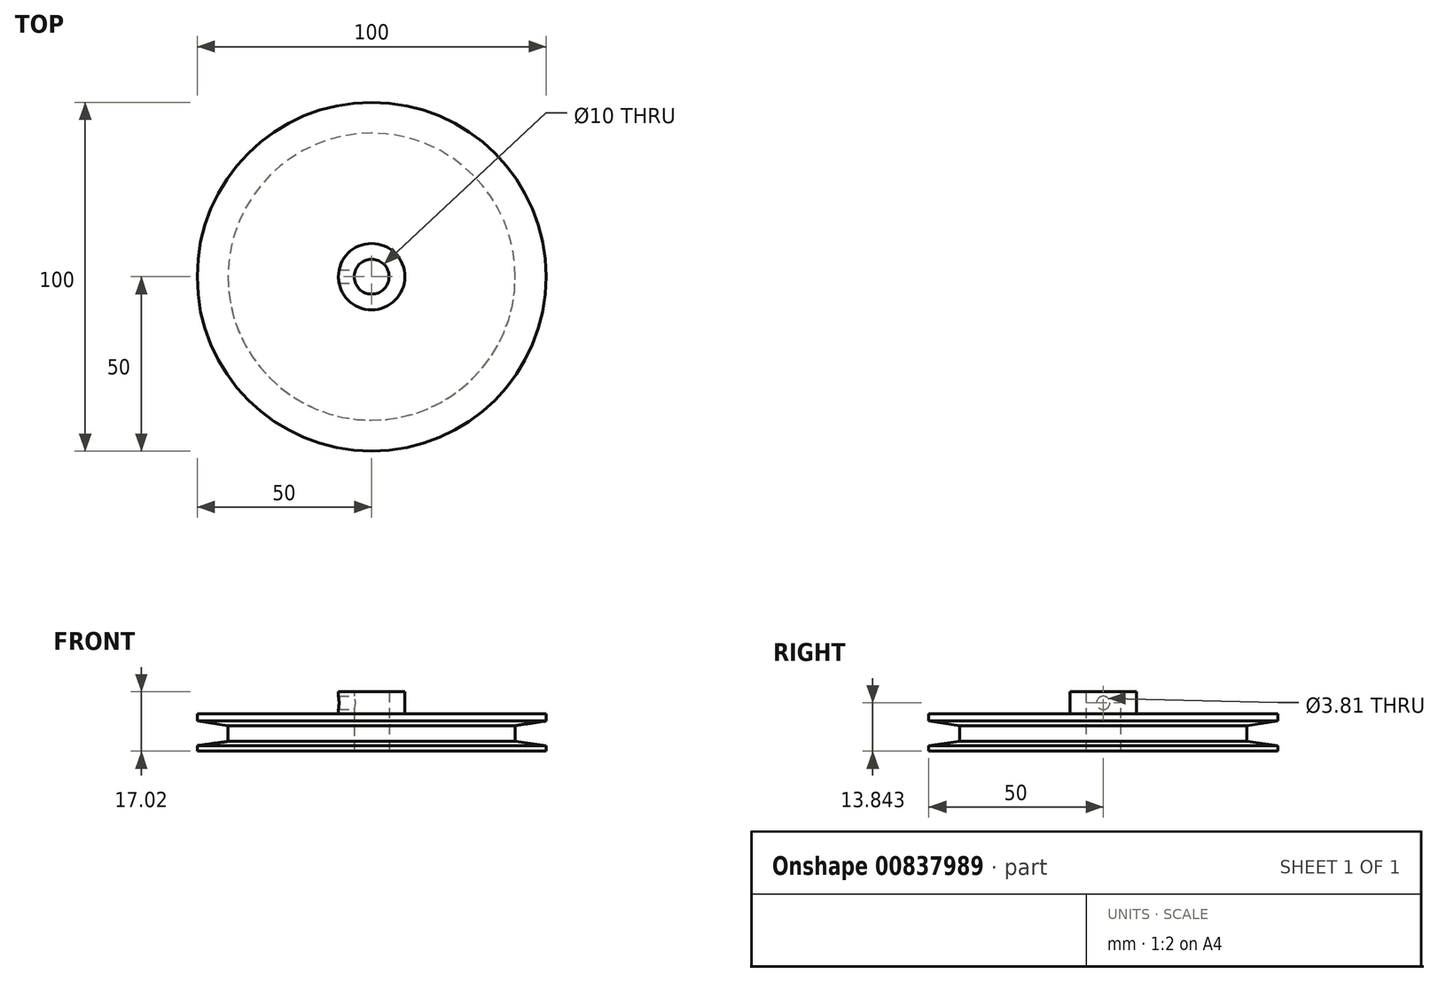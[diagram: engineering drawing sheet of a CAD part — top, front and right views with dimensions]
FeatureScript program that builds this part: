
annotation { "Feature Type Name" : "Feature", "Feature Type Description" : "" }
export const myFeature = defineFeature(function(context is Context, id is Id, definition is map)
    precondition{}
    {
        {
            var Q0;
            Q0=qCreatedBy(makeId("Top.planeOp"),FACE);
            var sketch = newSketch(context, id + "F0", { "sketchPlane" : qUnion([Q0])});
            skCircle(sketch, "E0", {"center": v(0, 0) * mm, "radius": 50 * mm});
            skSolve(sketch);
        }
        {
            var Q0;
            Q0=makeQuery(id+"F0.imprint","IMPRINT",FACE,{"disambiguationData":[TD([[makeQuery(id+"F0.imprint","IMPRINT",EDGE,{"derivedFrom":sQuery(id+"F0.wireOp",EDGE,"E0")}),1.0]])]});
            extrude(context, id + "F1", {"entities" : qUnion([Q0]), "depth" : 10.67 * mm, "offsetDistance" : 25.4 * mm});
        }
        {
            var Q0;
            Q0=makeQuery(id+"F1.opExtrude","CAP_FACE",FACE,{"disambiguationData":[OSD([sQuery(id+"F0.wireOp",EDGE,"E0")])],"isStart":false});
            var sketch = newSketch(context, id + "F2", { "sketchPlane" : qUnion([Q0])});
            skCircle(sketch, "E1", {"center": v(0, 0) * mm, "radius": 9.53 * mm});
            skSolve(sketch);
        }
        {
            var Q0;
            Q0=makeQuery(id+"F2.imprint","IMPRINT",FACE,{"disambiguationData":[TD([[makeQuery(id+"F2.imprint","IMPRINT",EDGE,{"derivedFrom":sQuery(id+"F2.wireOp",EDGE,"E1")}),1.0]])]});
            extrude(context, id + "F3", {"entities" : qUnion([Q0]), "operationType" : NewBodyOperationType.ADD, "depth" : 6.35 * mm, "offsetDistance" : 25.4 * mm});
        }
        {
            var Q0;
            Q0=qCreatedBy(makeId("Right.planeOp"),FACE);
            var sketch = newSketch(context, id + "F4", { "sketchPlane" : qUnion([Q0])});
            skCircle(sketch, "E2", {"center": v(0, 13.84) * mm, "radius": 1.9 * mm});
            skSolve(sketch);
        }
        {
            var Q0;
            Q0=qSketchRegion(id+"F4",true);
            extrude(context, id + "F5", {"entities" : qUnion([Q0]), "operationType" : NewBodyOperationType.REMOVE, "oppositeDirection" : true, "depth" : 25.4 * mm, "offsetDistance" : 25.4 * mm});
        }
        {
            var Q0;
            Q0=makeQuery(id+"F1.opExtrude","CAP_FACE",FACE,{"disambiguationData":[OSD([sQuery(id+"F0.wireOp",EDGE,"E0")])],"isStart":true});
            var sketch = newSketch(context, id + "F6", { "sketchPlane" : qUnion([Q0])});
            skCircle(sketch, "E3", {"center": v(0, 0) * mm, "radius": 5 * mm});
            skSolve(sketch);
        }
        {
            var Q0;
            Q0=makeQuery(id+"F6.imprint","IMPRINT",FACE,{"disambiguationData":[TD([[makeQuery(id+"F6.imprint","IMPRINT",EDGE,{"derivedFrom":sQuery(id+"F6.wireOp",EDGE,"E3")}),1.0]])]});
            extrude(context, id + "F7", {"entities" : qUnion([Q0]), "operationType" : NewBodyOperationType.REMOVE, "oppositeDirection" : true, "depth" : 101.6 * mm, "offsetDistance" : 25.4 * mm});
        }
        {
            var Q0;
            Q0=qCreatedBy(makeId("Right.planeOp"),FACE);
            var sketch = newSketch(context, id + "F8", { "sketchPlane" : qUnion([Q0])});
            skArc(sketch, "E4", {"start": v(-50.07, 7.5) * mm, "mid": v(-51.77, 5.12) * mm, "end": v(-50.04, 2.75) * mm});
            skLineSegment(sketch, "E5", {"start": v(-50.07, 7.5) * mm, "end": v(-50.07, 8.68) * mm});
            skLineSegment(sketch, "E6", {"start": v(-50.04, 2.75) * mm, "end": v(-50.04, 1.58) * mm});
            skLineSegment(sketch, "E7", {"start": v(-41.15, 7.3) * mm, "end": v(-41.15, 2.78) * mm});
            skPoint(sketch, "E8.end.orphan", {"position": v(-41.15, 5.13) * mm});
            skLineSegment(sketch, "E9", {"start": v(-50.07, 8.68) * mm, "end": v(-41.15, 7.3) * mm});
            skLineSegment(sketch, "E10", {"start": v(-50.04, 1.58) * mm, "end": v(-41.15, 2.78) * mm});
            skPoint(sketch, "E11.end.orphan", {"position": v(-41.15, 8.68) * mm});
            skPoint(sketch, "E12.orphan", {"position": v(-41.15, 1.58) * mm});
            skSolve(sketch);
        }
        {
            var Q0;
            Q0=makeQuery(id+"F8.imprint","IMPRINT",FACE,{"disambiguationData":[TD([[makeQuery(id+"F8.imprint","IMPRINT",EDGE,{"derivedFrom":sQuery(id+"F8.wireOp",EDGE,"E4")}),1.0]])]});
            var Q1;
            Q1=makeQuery(id+"F3.opExtrude","CAP_EDGE",EDGE,{"disambiguationData":[OSD([sQuery(id+"F2.wireOp",EDGE,"E1")])],"isStart":false});
            revolve(context, id + "F9", {"operationType" : NewBodyOperationType.REMOVE, "surfaceOperationType" : NewSurfaceOperationType.NEW, "entities" : qUnion([Q0]), "axis" : qUnion([Q1]), "revolveType" : RevolveType.FULL, "oppositeDirection" : true});
        }
    });
